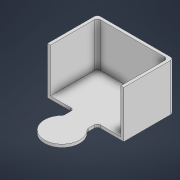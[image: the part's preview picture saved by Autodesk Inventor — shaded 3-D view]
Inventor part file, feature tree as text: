
AUTODESK INVENTOR PART (.ipt)
format: ipt  version: 2022 (Build 260153000, 153)  size: 140,800 bytes
history: native  units: in
note: dims shown in document units (in); Inventor stores cm internally (conversion verified against a paired STEP export)
features: extrude x2, fillet x2, sketch x2
ambient origin geometry x8: Origin, YZ Plane, XZ Plane, XY Plane, X Axis, Y Axis, Z Axis, Center Point
bodies: Body1 (feature_tree)
feature tree (6):
  extrude  "Extrusion2"  Depth=2.0in
  fillet  "Fillet2"  Radius=1.0in
  extrude  "Extrusion3"  Depth=1.0in
  fillet  "Fillet3"  Radius=1.5in
  sketch  "Sketch1"  dims[d0=3.0in d1=2.0in d2=1.0in]
  sketch  "Sketch2"  dims[d3=1.0in d4=1.0in d5=1.5in d9=0.125in d10=0.0in d11=0.125in d12=0.125in d13=0.125in d14=0.125in d15=2.0in d16=0.0in d17=0.125in]
